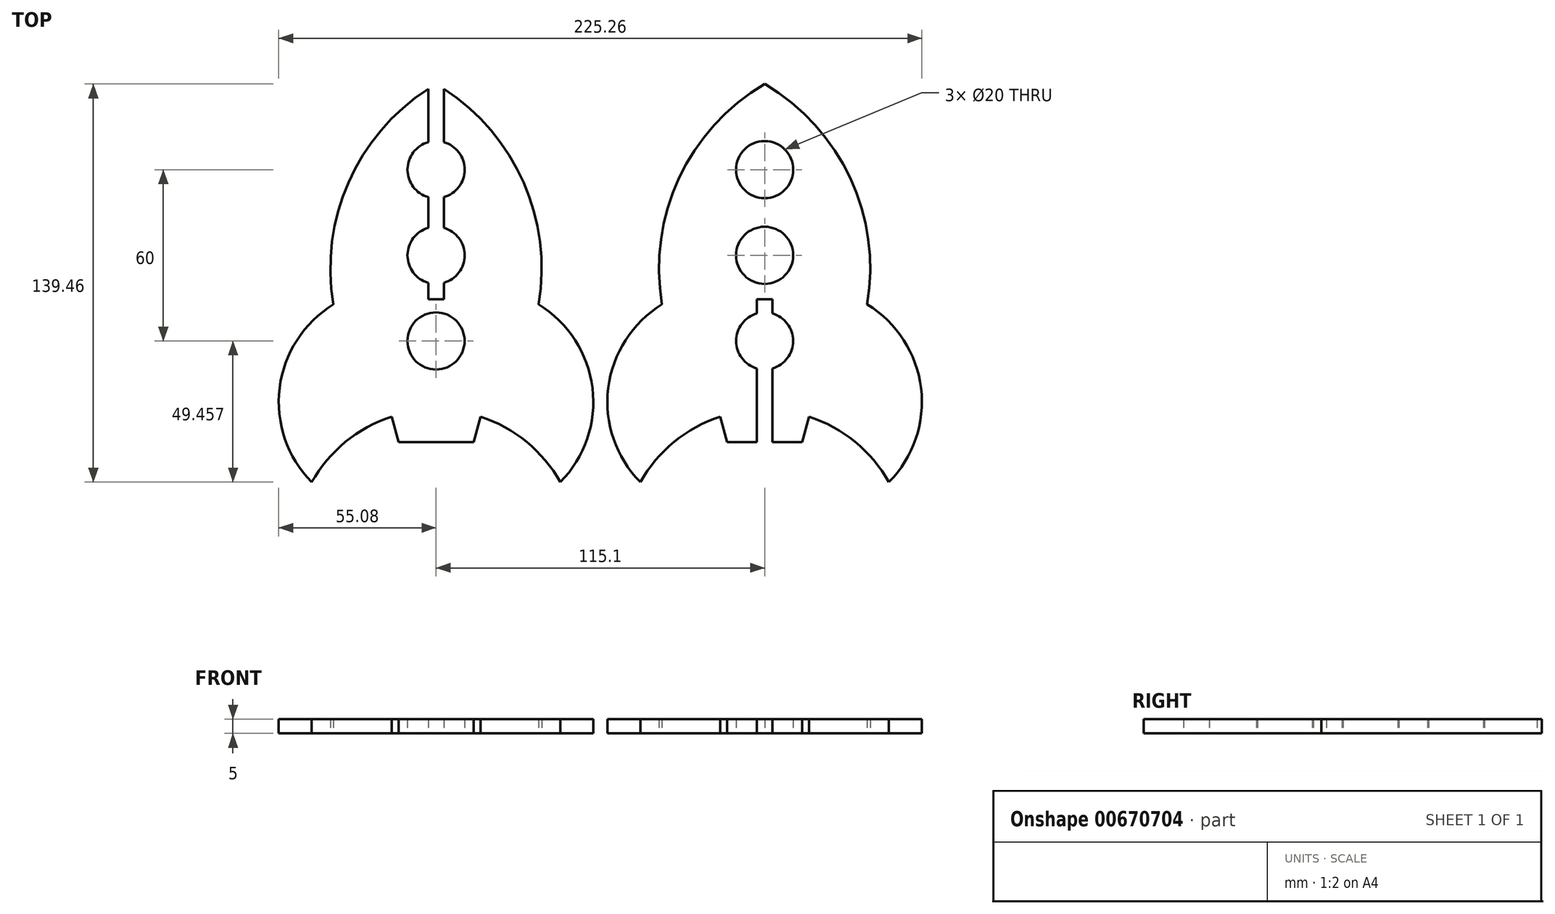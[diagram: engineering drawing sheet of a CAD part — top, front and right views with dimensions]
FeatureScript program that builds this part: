
annotation { "Feature Type Name" : "Feature", "Feature Type Description" : "" }
export const myFeature = defineFeature(function(context is Context, id is Id, definition is map)
    precondition{}
    {
        {
            var Q0;
            Q0=qCreatedBy(makeId("Top.planeOp"),FACE);
            var sketch = newSketch(context, id + "F0", { "sketchPlane" : qUnion([Q0])});
            skArc(sketch, "E0", {"start": v(43.55, -57.1) * mm, "mid": v(31.72, -43.01) * mm, "end": v(15.58, -34.15) * mm});
            skLineSegment(sketch, "E1", {"start": v(0, 96.78) * mm, "end": v(0, -116.58) * mm, "construction": true});
            skArc(sketch, "E2.trimOffspring", {"start": v(35.94, 5.13) * mm, "mid": v(30, 49.34) * mm, "end": v(0, 82.36) * mm});
            skArc(sketch, "E3.trimOffspring", {"start": v(43.55, -57.1) * mm, "mid": v(54.79, -24.15) * mm, "end": v(35.94, 5.13) * mm});
            skCircle(sketch, "E4", {"center": v(0, 52.36) * mm, "radius": 10 * mm});
            skCircle(sketch, "E5", {"center": v(0, 22.36) * mm, "radius": 10 * mm});
            skCircle(sketch, "E6", {"center": v(0, -7.64) * mm, "radius": 10 * mm});
            skLineSegment(sketch, "E7", {"start": v(15.58, -34.15) * mm, "end": v(13.14, -43.07) * mm});
            skLineSegment(sketch, "E8", {"start": v(13.14, -43.07) * mm, "end": v(0, -43.07) * mm});
            skLineSegment(sketch, "E9.MirrorCS", {"start": v(-15.58, -34.15) * mm, "end": v(-13.14, -43.07) * mm});
            skLineSegment(sketch, "E10.MirrorCS", {"start": v(-13.14, -43.07) * mm, "end": v(0, -43.07) * mm});
            skArc(sketch, "E11.MirrorCS", {"start": v(-43.55, -57.1) * mm, "mid": v(-31.72, -43.01) * mm, "end": v(-15.58, -34.15) * mm});
            skArc(sketch, "E12.MirrorCS", {"start": v(-43.55, -57.1) * mm, "mid": v(-54.79, -24.15) * mm, "end": v(-35.94, 5.13) * mm});
            skArc(sketch, "E13.MirrorCS", {"start": v(-35.94, 5.13) * mm, "mid": v(-30, 49.34) * mm, "end": v(0, 82.36) * mm});
            skLineSegment(sketch, "E14.bottom", {"start": v(2.75, -100) * mm, "end": v(-2.75, -100) * mm});
            skLineSegment(sketch, "E14.top", {"start": v(2.75, 100) * mm, "end": v(-2.75, 100) * mm});
            skLineSegment(sketch, "E14.left", {"start": v(2.75, -100) * mm, "end": v(2.75, 100) * mm});
            skLineSegment(sketch, "E14.right", {"start": v(-2.75, -100) * mm, "end": v(-2.75, 100) * mm});
            skPoint(sketch, "E14.middle", {"position": v(0, 0) * mm});
            skLineSegment(sketch, "E15", {"start": v(-2.75, 6.91) * mm, "end": v(2.75, 6.91) * mm});
            skSolve(sketch);
        }
        {
            var Q0;
            {var subQ11=sQuery(id+"F0.wireOp",EDGE,"E9.MirrorCS");Q0=makeQuery(id+"F0.imprint","IMPRINT",FACE,{"disambiguationData":[TD([[makeQuery(id+"F0.imprint","IMPRINT",EDGE,{"derivedFrom":subQ11}),1.0]])]});}
            var Q1;
            Q1=makeQuery(id+"F0.imprint","IMPRINT",FACE,{"disambiguationData":[TD([[makeQuery(id+"F0.imprint","IMPRINT",EDGE,{"derivedFrom":sQuery(id+"F0.wireOp",EDGE,"E0")}),-1.0]])]});
            var Q2;
            {var subQ3=sQuery(id+"F0.wireOp",EDGE,"E14.right");var subQ7=sQuery(id+"F0.wireOp",EDGE,"E6");var subQ9=makeQuery(id+"F0.imprint","INTERSECT",VERTEX,{"disambiguationData":[OD(1.0)],"derivedFrom":[subQ7,subQ3]});Q2=makeQuery(id+"F0.imprint","IMPRINT",FACE,{"disambiguationData":[TD([[makeQuery(id+"F0.imprint","IMPRINT",EDGE,{"disambiguationData":[TD([[subQ9,-1.0]])],"derivedFrom":subQ7}),-1.0]])]});}
            var Q3;
            {var subQ5=sQuery(id+"F0.wireOp",EDGE,"E15");Q3=makeQuery(id+"F0.imprint","IMPRINT",FACE,{"disambiguationData":[TD([[makeQuery(id+"F0.imprint","IMPRINT",EDGE,{"derivedFrom":subQ5}),-1.0]])]});}
            extrude(context, id + "F1", {"entities" : qUnion([Q0, Q1, Q2, Q3]), "depth" : 5 * mm, "offsetDistance" : 25 * mm});
        }
        {
            var Q0;
            {var subQ11=sQuery(id+"F0.wireOp",EDGE,"E9.MirrorCS");Q0=makeQuery(id+"F0.imprint","IMPRINT",FACE,{"disambiguationData":[TD([[makeQuery(id+"F0.imprint","IMPRINT",EDGE,{"derivedFrom":subQ11}),1.0]])]});}
            var Q1;
            Q1=makeQuery(id+"F0.imprint","IMPRINT",FACE,{"disambiguationData":[TD([[makeQuery(id+"F0.imprint","IMPRINT",EDGE,{"derivedFrom":sQuery(id+"F0.wireOp",EDGE,"E0")}),-1.0]])]});
            var Q2;
            {var subQ1=sQuery(id+"F0.wireOp",EDGE,"E2.trimOffspring");var subQ5=sQuery(id+"F0.wireOp",EDGE,"E13.MirrorCS");var subQ6=makeQuery(id+"F0.imprint","INTERSECT",VERTEX,{"derivedFrom":[subQ1,subQ5]});Q2=makeQuery(id+"F0.imprint","IMPRINT",FACE,{"disambiguationData":[TD([[makeQuery(id+"F0.imprint","IMPRINT",EDGE,{"disambiguationData":[TD([[subQ6,1.0]])],"derivedFrom":subQ1}),1.0]])]});}
            var Q3;
            {var subQ0=sQuery(id+"F0.wireOp",EDGE,"E14.right");var subQ1=sQuery(id+"F0.wireOp",EDGE,"E4");var subQ2=makeQuery(id+"F0.imprint","INTERSECT",VERTEX,{"disambiguationData":[OD(1.0)],"derivedFrom":[subQ1,subQ0]});Q3=makeQuery(id+"F0.imprint","IMPRINT",FACE,{"disambiguationData":[TD([[makeQuery(id+"F0.imprint","IMPRINT",EDGE,{"disambiguationData":[TD([[subQ2,-1.0]])],"derivedFrom":subQ1}),-1.0]])]});}
            var Q4;
            {var subQ5=sQuery(id+"F0.wireOp",EDGE,"E15");Q4=makeQuery(id+"F0.imprint","IMPRINT",FACE,{"disambiguationData":[TD([[makeQuery(id+"F0.imprint","IMPRINT",EDGE,{"derivedFrom":subQ5}),1.0]])]});}
            extrude(context, id + "F2", {"entities" : qUnion([Q0, Q1, Q2, Q3, Q4]), "depth" : 5 * mm, "offsetDistance" : 25 * mm});
        }
        {
            var Q0;
            Q0=makeQuery(id+"F1.opExtrude","SWEPT_BODY",BODY,{"disambiguationData":[OSD([sQuery(id+"F0.wireOp",EDGE,"E0"),sQuery(id+"F0.wireOp",EDGE,"E2.trimOffspring"),sQuery(id+"F0.wireOp",EDGE,"E3.trimOffspring"),sQuery(id+"F0.wireOp",EDGE,"E4"),sQuery(id+"F0.wireOp",EDGE,"E5"),sQuery(id+"F0.wireOp",EDGE,"E6"),sQuery(id+"F0.wireOp",EDGE,"E7"),sQuery(id+"F0.wireOp",EDGE,"E8"),sQuery(id+"F0.wireOp",EDGE,"E9.MirrorCS"),sQuery(id+"F0.wireOp",EDGE,"E10.MirrorCS"),sQuery(id+"F0.wireOp",EDGE,"E11.MirrorCS"),sQuery(id+"F0.wireOp",EDGE,"E12.MirrorCS"),sQuery(id+"F0.wireOp",EDGE,"E13.MirrorCS"),sQuery(id+"F0.wireOp",EDGE,"E14.left"),sQuery(id+"F0.wireOp",EDGE,"E14.right"),sQuery(id+"F0.wireOp",EDGE,"E15")])]});
            transform(context, id + "F3", {"entities" : qUnion([Q0]), "transformType" : TransformType.TRANSLATION_3D, "dx" : -115.1 * mm, "dy" : 0 * mm, "dz" : 0 * mm, "makeCopy" : false});
        }
    });
